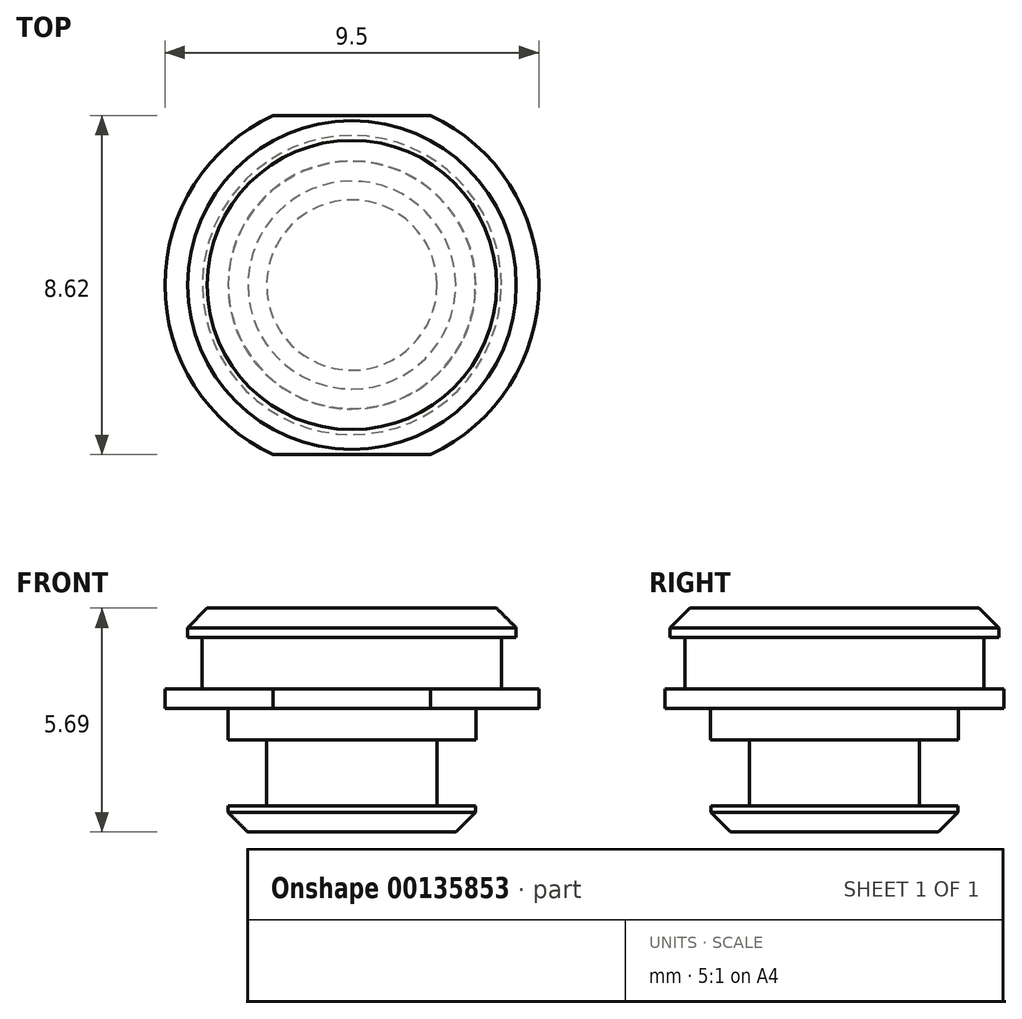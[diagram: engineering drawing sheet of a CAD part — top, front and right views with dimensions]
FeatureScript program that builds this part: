
annotation { "Feature Type Name" : "Feature", "Feature Type Description" : "" }
export const myFeature = defineFeature(function(context is Context, id is Id, definition is map)
    precondition{}
    {
        {
            var Q0;
            Q0=qCreatedBy(makeId("Top.planeOp"),FACE);
            var sketch = newSketch(context, id + "F0", { "sketchPlane" : qUnion([Q0])});
            skCircle(sketch, "E0", {"center": v(0, 0) * mm, "radius": 4.75 * mm});
            skSolve(sketch);
        }
        {
            var Q0;
            Q0 = qSketchRegion(id + "F0", true);
            extrude(context, id + "F1", {"entities" : qUnion([Q0]), "depth" : 0.5 * mm});
        }
        {
            var Q0;
            Q0=makeQuery(id+"F1.opExtrude","CAP_FACE",FACE,{"disambiguationData":[OSD([sQuery(id+"F0.wireOp",EDGE,"E0")])],"isStart":false});
            var sketch = newSketch(context, id + "F2", { "sketchPlane" : qUnion([Q0])});
            skCircle(sketch, "E1", {"center": v(0, 0) * mm, "radius": 3.8 * mm});
            skSolve(sketch);
        }
        {
            var Q0;
            Q0 = qSketchRegion(id + "F2", true);
            extrude(context, id + "F3", {"entities" : qUnion([Q0]), "operationType" : NewBodyOperationType.ADD, "depth" : 1.3 * mm});
        }
        {
            var Q0;
            Q0=makeQuery(id+"F3.opExtrude","CAP_FACE",FACE,{"disambiguationData":[OSD([sQuery(id+"F2.wireOp",EDGE,"E1")])],"isStart":false});
            var sketch = newSketch(context, id + "F4", { "sketchPlane" : qUnion([Q0])});
            skCircle(sketch, "E2.0", {"center": v(0, 0) * mm, "radius": 4.17 * mm});
            skSolve(sketch);
        }
        {
            var Q0;
            Q0=makeQuery(id+"F4.imprint","IMPRINT",FACE,{"disambiguationData":[TD([[makeQuery(id+"F4.imprint","IMPRINT",EDGE,{"derivedFrom":makeQuery(id+"F3.opExtrude","CAP_EDGE",EDGE,{"disambiguationData":[OSD([sQuery(id+"F2.wireOp",EDGE,"E1")])],"isStart":false})}),1.0]])]});
            var Q1;
            Q1=makeQuery(id+"F4.imprint","IMPRINT",FACE,{"disambiguationData":[TD([[makeQuery(id+"F4.imprint","IMPRINT",EDGE,{"derivedFrom":sQuery(id+"F4.wireOp",EDGE,"E2.0")}),1.0]])]});
            extrude(context, id + "F5", {"entities" : qUnion([Q0, Q1]), "operationType" : NewBodyOperationType.ADD, "depth" : 0.75 * mm});
        }
        {
            var Q0;
            Q0=makeQuery(id+"F5.opExtrude","CAP_EDGE",EDGE,{"disambiguationData":[OSD([sQuery(id+"F4.wireOp",EDGE,"E2.0")])],"isStart":false});
            chamfer(context, id + "F6", {"entities" : qUnion([Q0]), "width" : 0.5 * mm, "tangentPropagation" : true});
        }
        {
            var Q0;
            Q0=makeQuery(id+"F1.opExtrude","CAP_FACE",FACE,{"disambiguationData":[OSD([sQuery(id+"F0.wireOp",EDGE,"E0")])],"isStart":true});
            var sketch = newSketch(context, id + "F7", { "sketchPlane" : qUnion([Q0])});
            skLineSegment(sketch, "E3", {"start": v(0, 4.3) * mm, "end": v(-2, 4.3) * mm});
            skLineSegment(sketch, "E4", {"start": v(-2, 4.3) * mm, "end": v(2, 4.3) * mm});
            skLineSegment(sketch, "E5", {"start": v(0, -4.3) * mm, "end": v(2, -4.3) * mm});
            skLineSegment(sketch, "E6", {"start": v(2, -4.3) * mm, "end": v(-2, -4.3) * mm});
            skSolve(sketch);
        }
        {
            var Q0;
            Q0 = qSketchRegion(id + "F7", true);
            var Q1;
            {var subQ0=sQuery(id+"F7.wireOp",EDGE,"E4");var subQ3=makeQuery(id+"F7.imprint","IMPRINT",VERTEX,{"derivedFrom":subQ0});Q1=makeQuery(id+"F7.imprint","IMPRINT",FACE,{"disambiguationData":[TD([[makeQuery(id+"F7.imprint","IMPRINT",EDGE,{"disambiguationData":[TD([[subQ3,1.0]])],"derivedFrom":subQ0}),1.0]])]});}
            var Q2;
            {var subQ0=sQuery(id+"F7.wireOp",EDGE,"E6");var subQ3=makeQuery(id+"F7.imprint","IMPRINT",VERTEX,{"derivedFrom":subQ0});Q2=makeQuery(id+"F7.imprint","IMPRINT",FACE,{"disambiguationData":[TD([[makeQuery(id+"F7.imprint","IMPRINT",EDGE,{"disambiguationData":[TD([[subQ3,1.0]])],"derivedFrom":subQ0}),1.0]])]});}
            extrude(context, id + "F8", {"entities" : qUnion([Q0, Q1, Q2]), "operationType" : NewBodyOperationType.REMOVE, "endBound" : BoundingType.THROUGH_ALL, "oppositeDirection" : true, "depth" : 25 * mm});
        }
        {
            var Q0;
            Q0=makeQuery(id+"F1.opExtrude","CAP_FACE",FACE,{"disambiguationData":[OSD([sQuery(id+"F0.wireOp",EDGE,"E0")])],"isStart":true});
            var sketch = newSketch(context, id + "F9", { "sketchPlane" : qUnion([Q0])});
            skCircle(sketch, "E7", {"center": v(0, 0) * mm, "radius": 3.15 * mm});
            skSolve(sketch);
        }
        {
            var Q0;
            Q0 = qSketchRegion(id + "F9", true);
            extrude(context, id + "F10", {"entities" : qUnion([Q0]), "operationType" : NewBodyOperationType.ADD, "depth" : 0.8 * mm});
        }
        {
            var Q0;
            Q0=makeQuery(id+"F10.opExtrude","CAP_FACE",FACE,{"disambiguationData":[OSD([sQuery(id+"F9.wireOp",EDGE,"E7")])],"isStart":false});
            var sketch = newSketch(context, id + "F11", { "sketchPlane" : qUnion([Q0])});
            skCircle(sketch, "E8", {"center": v(0, 0) * mm, "radius": 2.17 * mm});
            skSolve(sketch);
        }
        {
            var Q0;
            Q0 = qSketchRegion(id + "F11", true);
            extrude(context, id + "F12", {"entities" : qUnion([Q0]), "operationType" : NewBodyOperationType.ADD, "depth" : 1.67 * mm});
        }
        {
            var Q0;
            Q0=makeQuery(id+"F12.opExtrude","CAP_FACE",FACE,{"disambiguationData":[OSD([sQuery(id+"F11.wireOp",EDGE,"E8")])],"isStart":false});
            var sketch = newSketch(context, id + "F13", { "sketchPlane" : qUnion([Q0])});
            skCircle(sketch, "E9.0", {"center": v(0, 0) * mm, "radius": 3.14 * mm});
            skSolve(sketch);
        }
        {
            var Q0;
            Q0 = qSketchRegion(id + "F13", true);
            extrude(context, id + "F14", {"entities" : qUnion([Q0]), "operationType" : NewBodyOperationType.ADD, "depth" : 0.67 * mm});
        }
        {
            var Q0;
            Q0=makeQuery(id+"F14.opExtrude","CAP_EDGE",EDGE,{"disambiguationData":[OSD([sQuery(id+"F13.wireOp",EDGE,"E9.0")])],"isStart":false});
            chamfer(context, id + "F15", {"entities" : qUnion([Q0]), "width" : 0.5 * mm, "tangentPropagation" : true});
        }
    });
